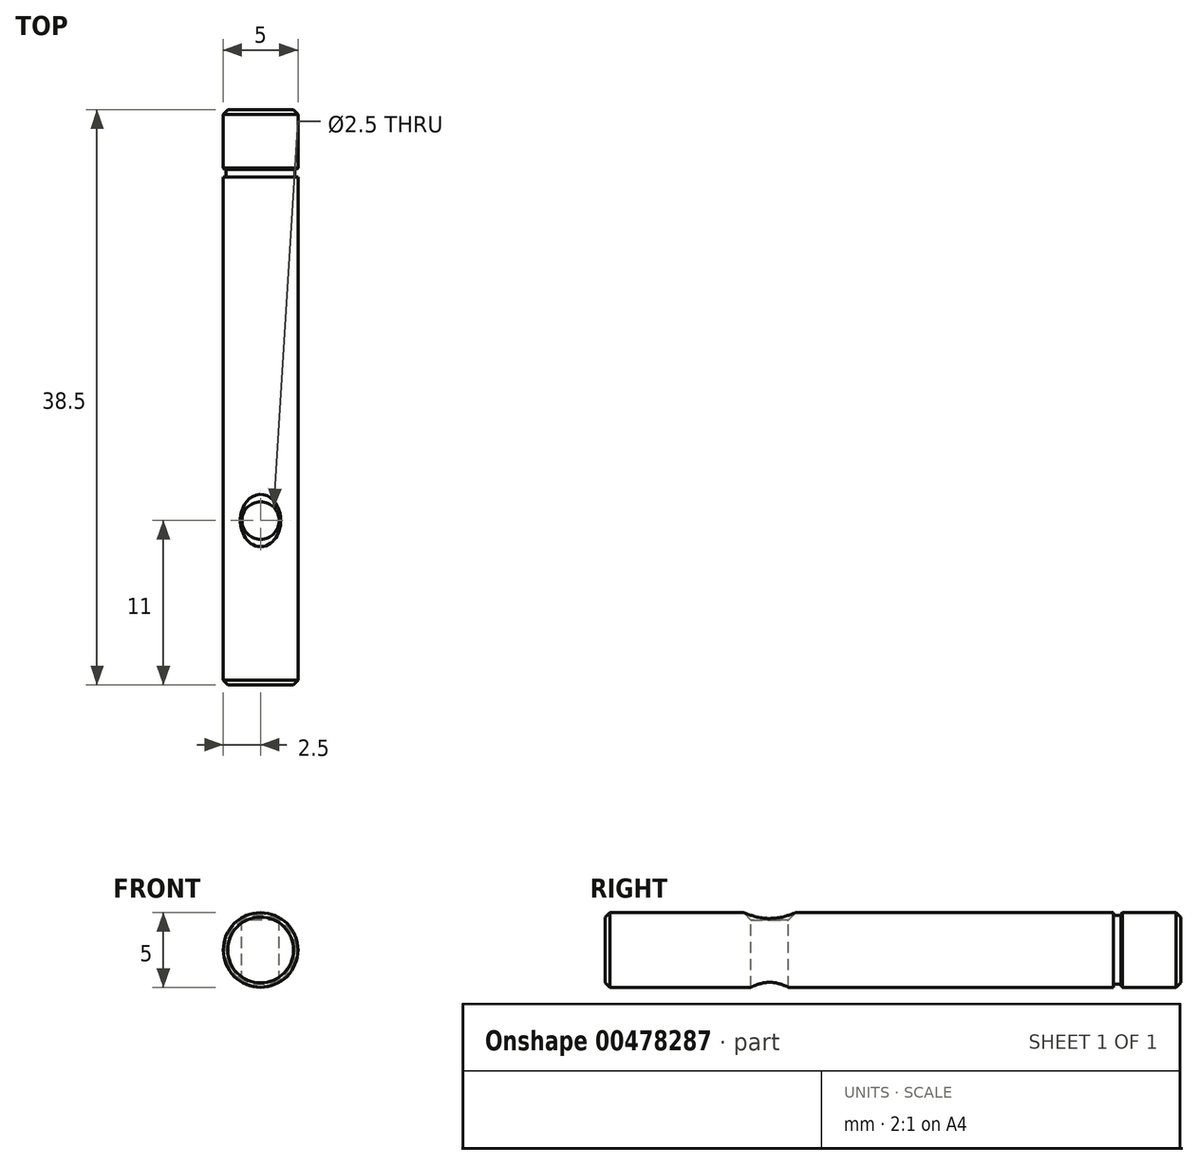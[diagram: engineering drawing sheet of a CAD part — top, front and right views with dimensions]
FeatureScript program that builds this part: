
annotation { "Feature Type Name" : "Feature", "Feature Type Description" : "" }
export const myFeature = defineFeature(function(context is Context, id is Id, definition is map)
    precondition{}
    {
        {
            var Q0;
            Q0=qCreatedBy(makeId("Front.planeOp"),FACE);
            var sketch = newSketch(context, id + "F0", { "sketchPlane" : qUnion([Q0])});
            skCircle(sketch, "E0", {"center": v(0, 0) * mm, "radius": 2.5 * mm});
            skCircle(sketch, "E1.0", {"center": v(0, 0) * mm, "radius": 2.3 * mm});
            skSolve(sketch);
        }
        {
            var Q0;
            Q0=makeQuery(id+"F0.imprint","IMPRINT",FACE,{"disambiguationData":[TD([[makeQuery(id+"F0.imprint","IMPRINT",EDGE,{"derivedFrom":sQuery(id+"F0.wireOp",EDGE,"E0")}),1.0]])]});
            var Q1;
            Q1=makeQuery(id+"F0.imprint","IMPRINT",FACE,{"disambiguationData":[TD([[makeQuery(id+"F0.imprint","IMPRINT",EDGE,{"derivedFrom":sQuery(id+"F0.wireOp",EDGE,"E1.0")}),1.0]])]});
            extrude(context, id + "F1", {"entities" : qUnion([Q0, Q1]), "depth" : 38.5 * mm});
        }
        {
            var Q0;
            Q0=makeQuery(id+"F1.opExtrude","CAP_EDGE",EDGE,{"disambiguationData":[OSD([sQuery(id+"F0.wireOp",EDGE,"E0")])],"isStart":false});
            var Q1;
            Q1=makeQuery(id+"F1.opExtrude","CAP_EDGE",EDGE,{"disambiguationData":[OSD([sQuery(id+"F0.wireOp",EDGE,"E0")])],"isStart":true});
            chamfer(context, id + "F2", {"entities" : qUnion([Q0, Q1]), "width" : 0.3 * mm, "tangentPropagation" : true});
        }
        {
            var Q0;
            Q0=qCreatedBy(makeId("Top.planeOp"),FACE);
            cPlane(context, id + "F3", {"entities" : qUnion([Q0]), "cplaneType" : CPlaneType.OFFSET, "offset" : 3 * mm, "width" : 150 * mm, "height" : 150 * mm});
        }
        {
            var Q0;
            Q0=qCreatedBy(id+"F3.planeOp",FACE);
            var sketch = newSketch(context, id + "F4", { "sketchPlane" : qUnion([Q0])});
            skPoint(sketch, "E2", {"position": v(0, -27.5) * mm});
            skLineSegment(sketch, "E3", {"start": v(0, 0) * mm, "end": v(0, -38.5) * mm, "construction": true});
            skSolve(sketch);
        }
        {
            var Q0;
            Q0=sQuery(id+"F4.wireOp",VERTEX,"E2");
            var Q1;
            Q1=makeQuery(id+"F1.opExtrude","SWEPT_BODY",BODY,{"disambiguationData":[OSD([sQuery(id+"F0.wireOp",EDGE,"E0")])]});
            hole(context, id + "F5", {"style" : HoleStyle.C_SINK, "endStyle" : HoleEndStyle.THROUGH, "holeDiameter" : 2.5 * mm, "cSinkDiameter" : 4.5 * mm, "cSinkAngle" : 90 * degree, "isTappedThrough" : true, "tappedDepth" : 12 * mm, "tapClearance" : 3, "startFromSketch" : true, "locations" : qUnion([Q0]), "scope" : qUnion([Q1])});
        }
        {
            var Q0;
            Q0=makeQuery(id+"F0.imprint","IMPRINT",FACE,{"disambiguationData":[TD([[makeQuery(id+"F0.imprint","IMPRINT",EDGE,{"derivedFrom":sQuery(id+"F0.wireOp",EDGE,"E0")}),1.0]])]});
            extrude(context, id + "F6", {"entities" : qUnion([Q0]), "operationType" : NewBodyOperationType.REMOVE, "depth" : 4.5 * mm, "hasSecondDirection" : true, "secondDirectionOppositeDirection" : false, "secondDirectionDepth" : 4 * mm});
        }
        {
            var Q0;
            Q0=makeQuery(id+"F6.boolean.opBoolean","COPY",EDGE,{"derivedFrom":makeQuery(id+"F6.opExtrude","CAP_EDGE",EDGE,{"disambiguationData":[OSD([sQuery(id+"F0.wireOp",EDGE,"E0")])],"isStart":true})});
            var Q1;
            Q1=makeQuery(id+"F6.boolean.opBoolean","COPY",EDGE,{"derivedFrom":makeQuery(id+"F6.opExtrude","CAP_EDGE",EDGE,{"disambiguationData":[OSD([sQuery(id+"F0.wireOp",EDGE,"E0")])],"isStart":false})});
            chamfer(context, id + "F7", {"entities" : qUnion([Q0, Q1]), "width" : 0.1 * mm, "tangentPropagation" : true});
        }
    });
